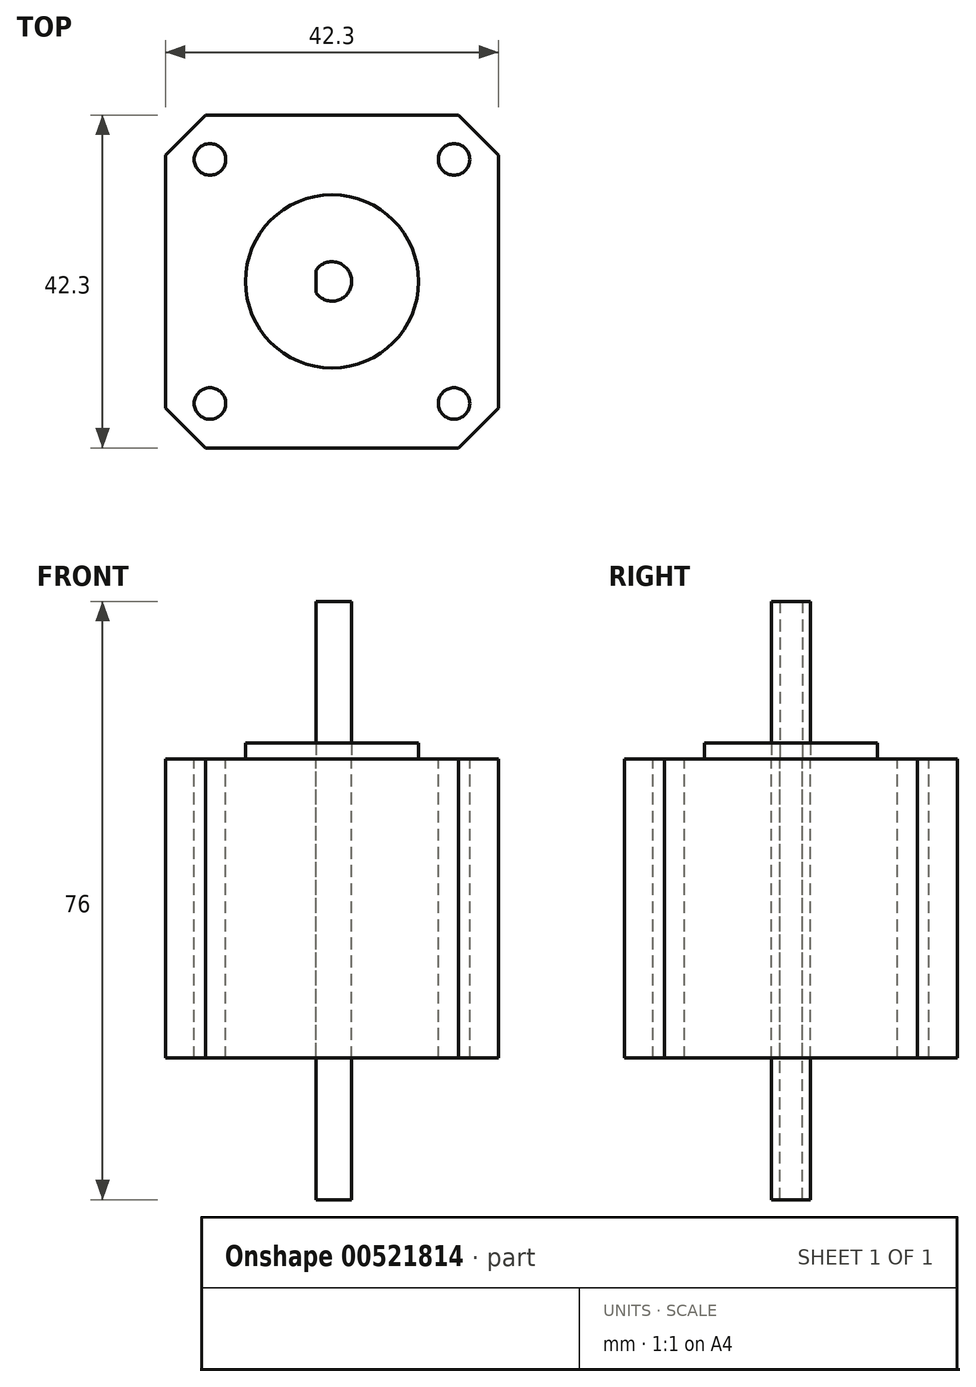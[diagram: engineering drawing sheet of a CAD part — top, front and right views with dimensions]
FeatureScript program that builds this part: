
annotation { "Feature Type Name" : "Feature", "Feature Type Description" : "" }
export const myFeature = defineFeature(function(context is Context, id is Id, definition is map)
    precondition{}
    {
        {
            var Q0;
            Q0=qCreatedBy(makeId("Top.planeOp"),FACE);
            var sketch = newSketch(context, id + "F0", { "sketchPlane" : qUnion([Q0])});
            skLineSegment(sketch, "E0.bottom", {"start": v(-21.15, 21.15) * mm, "end": v(21.15, 21.15) * mm});
            skLineSegment(sketch, "E0.top", {"start": v(-21.15, -21.15) * mm, "end": v(21.15, -21.15) * mm});
            skLineSegment(sketch, "E0.left", {"start": v(-21.15, 21.15) * mm, "end": v(-21.15, -21.15) * mm});
            skLineSegment(sketch, "E0.right", {"start": v(21.15, 21.15) * mm, "end": v(21.15, -21.15) * mm});
            skPoint(sketch, "E0.middle", {"position": v(0, 0) * mm});
            skLineSegment(sketch, "E1.bottom", {"start": v(-15.5, 15.5) * mm, "end": v(15.5, 15.5) * mm});
            skLineSegment(sketch, "E1.top", {"start": v(-15.5, -15.5) * mm, "end": v(15.5, -15.5) * mm});
            skLineSegment(sketch, "E1.left", {"start": v(-15.5, 15.5) * mm, "end": v(-15.5, -15.5) * mm});
            skLineSegment(sketch, "E1.right", {"start": v(15.5, 15.5) * mm, "end": v(15.5, -15.5) * mm});
            skCircle(sketch, "E2", {"center": v(-15.5, 15.5) * mm, "radius": 2 * mm});
            skCircle(sketch, "E3.MirrorC", {"center": v(15.5, 15.5) * mm, "radius": 2 * mm});
            skCircle(sketch, "E4.MirrorC", {"center": v(-15.5, -15.5) * mm, "radius": 2 * mm});
            skCircle(sketch, "E5.MirrorC", {"center": v(15.5, -15.5) * mm, "radius": 2 * mm});
            skCircle(sketch, "E6", {"center": v(0, 0) * mm, "radius": 11 * mm});
            skArc(sketch, "E7", {"start": v(-2.05, -1.43) * mm, "mid": v(2.5, 0) * mm, "end": v(-2.05, 1.43) * mm});
            skLineSegment(sketch, "E8", {"start": v(-2.05, 1.43) * mm, "end": v(-2.05, -1.43) * mm});
            skPoint(sketch, "E9", {"position": v(2.5, 0) * mm});
            skSolve(sketch);
        }
        {
            var Q0;
            Q0=makeQuery(id+"F0.imprint","IMPRINT",FACE,{"disambiguationData":[TD([[makeQuery(id+"F0.imprint","IMPRINT",EDGE,{"derivedFrom":sQuery(id+"F0.wireOp",EDGE,"E7")}),1.0]])]});
            extrude(context, id + "F1", {"entities" : qUnion([Q0]), "depth" : 20 * mm, "offsetDistance" : 25.4 * mm});
        }
        {
            var Q0;
            Q0=makeQuery(id+"F0.imprint","IMPRINT",FACE,{"disambiguationData":[TD([[makeQuery(id+"F0.imprint","IMPRINT",EDGE,{"derivedFrom":sQuery(id+"F0.wireOp",EDGE,"E6")}),1.0]])]});
            var Q1;
            Q1=makeQuery(id+"F0.imprint","IMPRINT",FACE,{"disambiguationData":[TD([[makeQuery(id+"F0.imprint","IMPRINT",EDGE,{"derivedFrom":sQuery(id+"F0.wireOp",EDGE,"E0.bottom")}),-1.0]])]});
            var Q2;
            Q2=makeQuery(id+"F0.imprint","IMPRINT",FACE,{"disambiguationData":[TD([[makeQuery(id+"F0.imprint","IMPRINT",EDGE,{"derivedFrom":sQuery(id+"F0.wireOp",EDGE,"E6")}),-1.0]])]});
            extrude(context, id + "F2", {"entities" : qUnion([Q0, Q1, Q2]), "oppositeDirection" : true, "depth" : 38 * mm, "offsetDistance" : 25.4 * mm});
        }
        {
            var Q0;
            Q0=makeQuery(id+"F0.imprint","IMPRINT",FACE,{"disambiguationData":[TD([[makeQuery(id+"F0.imprint","IMPRINT",EDGE,{"derivedFrom":sQuery(id+"F0.wireOp",EDGE,"E6")}),1.0]])]});
            extrude(context, id + "F3", {"entities" : qUnion([Q0]), "depth" : 2 * mm, "offsetDistance" : 25.4 * mm});
        }
        {
            var Q0;
            Q0=makeQuery(id+"F0.imprint","IMPRINT",FACE,{"disambiguationData":[TD([[makeQuery(id+"F0.imprint","IMPRINT",EDGE,{"derivedFrom":sQuery(id+"F0.wireOp",EDGE,"E7")}),1.0]])]});
            var Q1;
            Q1=makeQuery(id+"F2.opExtrude","CAP_FACE",FACE,{"disambiguationData":[OSD([sQuery(id+"F0.wireOp",EDGE,"E0.bottom"),sQuery(id+"F0.wireOp",EDGE,"E0.top"),sQuery(id+"F0.wireOp",EDGE,"E0.left"),sQuery(id+"F0.wireOp",EDGE,"E0.right"),sQuery(id+"F0.wireOp",EDGE,"E3.MirrorC"),sQuery(id+"F0.wireOp",EDGE,"E2"),sQuery(id+"F0.wireOp",EDGE,"E4.MirrorC"),sQuery(id+"F0.wireOp",EDGE,"E5.MirrorC"),sQuery(id+"F0.wireOp",EDGE,"E7"),sQuery(id+"F0.wireOp",EDGE,"E8")])],"isStart":false});
            extrude(context, id + "F4", {"entities" : qUnion([Q0]), "oppositeDirection" : true, "depth" : 56 * mm, "endBoundEntityFace" : qUnion([Q1]), "offsetDistance" : 25.4 * mm});
        }
        {
            var Q0;
            Q0=makeQuery(id+"F2.opExtrude","SWEPT_EDGE",EDGE,{"disambiguationData":[OSD([sQuery(id+"F0.wireOp",EDGE,"E0.bottom"),sQuery(id+"F0.wireOp",EDGE,"E0.left")])]});
            var Q1;
            Q1=makeQuery(id+"F2.opExtrude","SWEPT_EDGE",EDGE,{"disambiguationData":[OSD([sQuery(id+"F0.wireOp",EDGE,"E0.bottom"),sQuery(id+"F0.wireOp",EDGE,"E0.right")])]});
            var Q2;
            Q2=makeQuery(id+"F2.opExtrude","SWEPT_EDGE",EDGE,{"disambiguationData":[OSD([sQuery(id+"F0.wireOp",EDGE,"E0.top"),sQuery(id+"F0.wireOp",EDGE,"E0.right")])]});
            var Q3;
            Q3=makeQuery(id+"F2.opExtrude","SWEPT_EDGE",EDGE,{"disambiguationData":[OSD([sQuery(id+"F0.wireOp",EDGE,"E0.top"),sQuery(id+"F0.wireOp",EDGE,"E0.left")])]});
            chamfer(context, id + "F5", {"entities" : qUnion([Q0, Q1, Q2, Q3]), "width" : 5.08 * mm, "tangentPropagation" : true});
        }
    });
